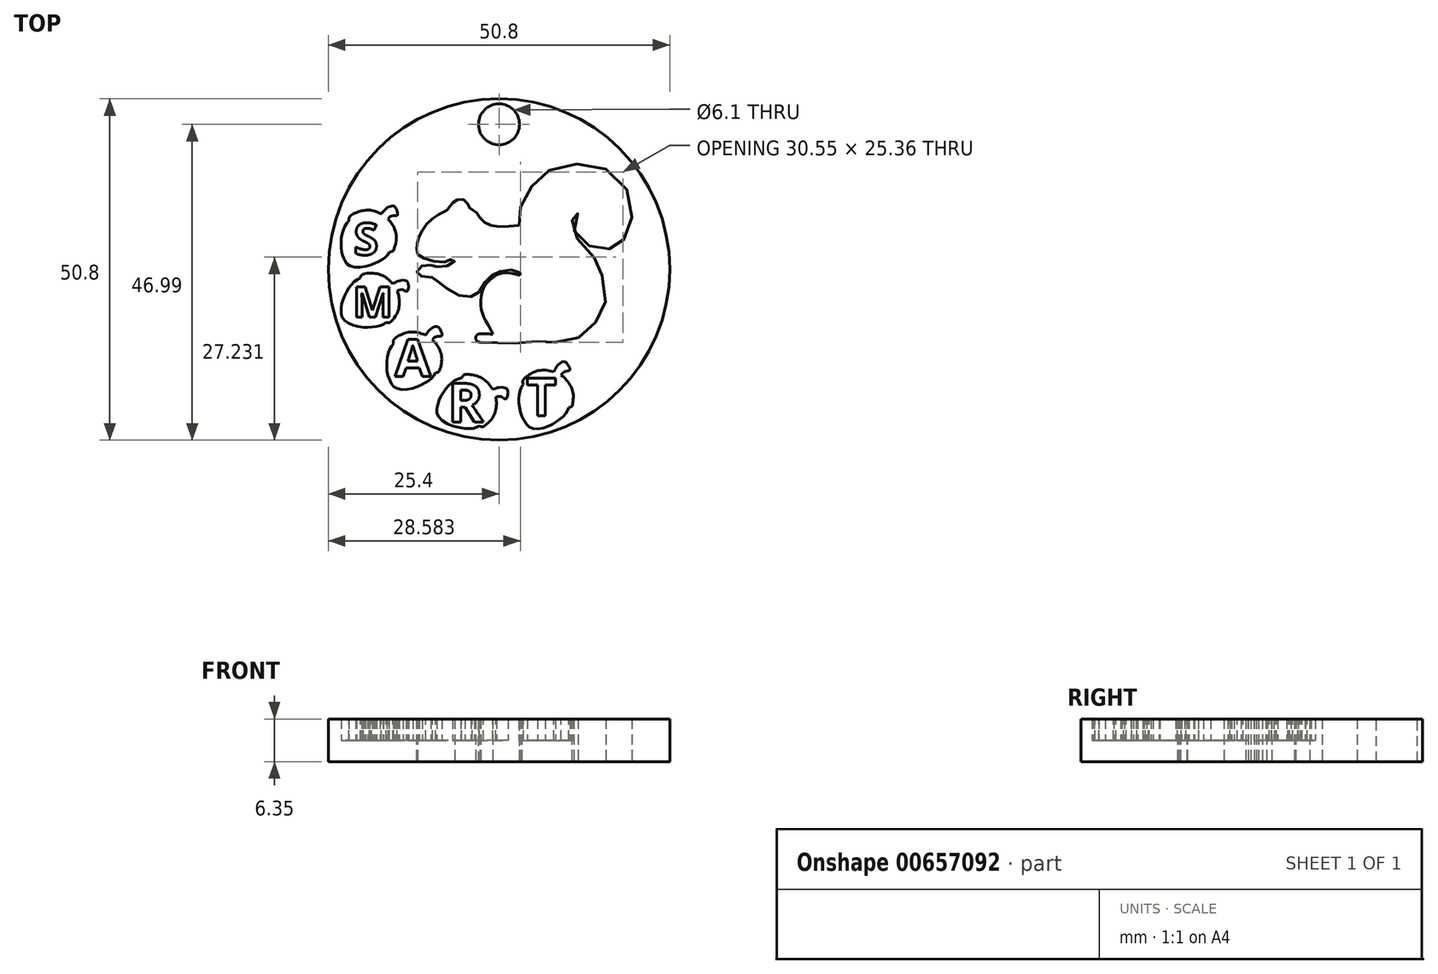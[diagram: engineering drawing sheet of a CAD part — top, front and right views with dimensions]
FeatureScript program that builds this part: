
annotation { "Feature Type Name" : "Feature", "Feature Type Description" : "" }
export const myFeature = defineFeature(function(context is Context, id is Id, definition is map)
    precondition{}
    {
        {
            var Q0;
            Q0=qCreatedBy(makeId("Top.planeOp"),FACE);
            var sketch = newSketch(context, id + "F0", { "sketchPlane" : qUnion([Q0])});
            skCircle(sketch, "E0", {"center": v(0, 0) * mm, "radius": 25.4 * mm});
            skFitSpline(sketch, "E1", {"points": [v(-12.1, 2.2) * mm, v(-12.26, 3.49) * mm, v(-11.69, 5.28) * mm, v(-10.34, 7.17) * mm, v(-8.41, 8.45) * mm, v(-7.87, 8.72) * mm, v(-7.27, 9.36) * mm, v(-6.8, 10) * mm, v(-5.44, 10.44) * mm, v(-4.57, 9.57) * mm, v(-4.2, 8.96) * mm, v(-3.55, 8.65) * mm, v(-2.64, 7.44) * mm, v(-0.82, 6.46) * mm, v(3, 6.53) * mm], "startDerivative": vector(-4.49, 18.18) * mm, "endDerivative": vector(35.45, 3.48) * mm});
            skFitSpline(sketch, "E2", {"points": [v(3, 6.53) * mm, v(3, 7.5) * mm, v(3.44, 10.07) * mm, v(4.79, 12.27) * mm, v(6.64, 14.3) * mm, v(10.15, 15.5) * mm, v(14.4, 15.47) * mm, v(18.15, 13.18) * mm, v(19.64, 9.63) * mm, v(19.47, 6.02) * mm, v(18.25, 4.06) * mm, v(17.1, 3.22) * mm, v(15.28, 3.02) * mm, v(13.33, 3.52) * mm, v(11.47, 5.08) * mm, v(11.17, 6.97) * mm, v(11.7, 8.28) * mm, v(11.74, 8.62) * mm, v(11.27, 8.32) * mm, v(10.8, 6.53) * mm, v(11.33, 4.97) * mm, v(13.66, 2.51) * mm, v(14.66, 0.7) * mm, v(15.42, -1.11) * mm, v(15.85, -4.65) * mm, v(15.06, -6.96) * mm, v(12.99, -9.3) * mm, v(11.24, -10.37) * mm, v(8.3, -10.88) * mm, v(6.28, -10.61) * mm, v(5.44, -10.76) * mm, v(3, -11) * mm, v(-2.86, -10.85) * mm], "startDerivative": vector(-1.3, 41.62) * mm, "endDerivative": vector(-127.9, 5.74) * mm});
            skFitSpline(sketch, "E3", {"points": [v(-2.86, -10.85) * mm, v(-3.36, -10.56) * mm, v(-3.44, -10.02) * mm, v(-3.08, -9.63) * mm, v(-0.95, -9.66) * mm], "startDerivative": vector(-2.88, 1) * mm, "endDerivative": vector(6.46, -0.66) * mm});
            skFitSpline(sketch, "E4", {"points": [v(-0.95, -9.66) * mm, v(-1.26, -8.87) * mm, v(-2.03, -7.56) * mm, v(-2.7, -5.53) * mm, v(-2.46, -3.21) * mm, v(-1.57, -1.76) * mm, v(0.43, -0.54) * mm, v(3.1, -0.87) * mm], "startDerivative": vector(-2.6, 7.91) * mm, "endDerivative": vector(16.1, -4.46) * mm});
            skFitSpline(sketch, "E5", {"points": [v(3.1, -0.87) * mm, v(3.4, -0.87) * mm, v(3.17, -0.52) * mm, v(2.19, -0.11) * mm, v(0.5, -0.25) * mm, v(-0.67, -0.67) * mm, v(-1.58, -1.23) * mm, v(-2.59, -2.8) * mm, v(-3.43, -3.82) * mm, v(-4.92, -4.09) * mm, v(-7.22, -3.22) * mm, v(-8.96, -1.9) * mm, v(-9.75, -1.34) * mm, v(-9.98, -1.15) * mm, v(-11.67, -1) * mm, v(-12.2, -0.62) * mm, v(-12.1, 0) * mm, v(-11.24, 0.62) * mm, v(-10.22, 0.64) * mm, v(-9.87, 0.47) * mm, v(-8.53, 0.45) * mm, v(-7.47, 0.62) * mm, v(-6.62, 1.2) * mm, v(-6.67, 1.53) * mm, v(-7.34, 1.44) * mm, v(-7.75, 1.16) * mm, v(-8.88, 1.09) * mm, v(-10.64, 1.47) * mm, v(-11.56, 1.85) * mm, v(-12.1, 2.2) * mm], "startDerivative": vector(20.9, -3.92) * mm, "endDerivative": vector(-18.16, 13.33) * mm});
            skSolve(sketch);
        }
        {
            var Q0;
            Q0=makeQuery(id+"F0.imprint","IMPRINT",FACE,{"disambiguationData":[TD([[makeQuery(id+"F0.imprint","IMPRINT",EDGE,{"derivedFrom":sQuery(id+"F0.wireOp",EDGE,"E0")}),1.0]])]});
            extrude(context, id + "F1", {"entities" : qUnion([Q0]), "depth" : 6.35 * mm, "offsetDistance" : 25.4 * mm});
        }
        {
            var Q0;
            Q0=makeQuery(id+"F1.opExtrude","CAP_FACE",FACE,{"disambiguationData":[OSD([sQuery(id+"F0.wireOp",EDGE,"E0"),sQuery(id+"F0.wireOp",EDGE,"E1"),sQuery(id+"F0.wireOp",EDGE,"E2"),sQuery(id+"F0.wireOp",EDGE,"E3"),sQuery(id+"F0.wireOp",EDGE,"E4"),sQuery(id+"F0.wireOp",EDGE,"E5")])],"isStart":false});
            var sketch = newSketch(context, id + "F2", { "sketchPlane" : qUnion([Q0])});
            skFitSpline(sketch, "E6", {"points": [v(-15.8, -2.16) * mm, v(-15.28, -1.87) * mm, v(-14.65, -1.64) * mm, v(-13.89, -1.64) * mm, v(-13.58, -1.89) * mm, v(-13.46, -2.26) * mm, v(-13.46, -2.78) * mm, v(-13.62, -3.2) * mm, v(-13.85, -3.24) * mm, v(-14.19, -3.08) * mm, v(-14.68, -3.02) * mm, v(-15.15, -3.22) * mm], "startDerivative": vector(4.96, 3.06) * mm, "endDerivative": vector(-4.83, -2.81) * mm});
            skFitSpline(sketch, "E7", {"points": [v(-15.15, -3.22) * mm, v(-15.03, -3.57) * mm, v(-14.85, -4.35) * mm, v(-14.86, -5.52) * mm, v(-15.15, -6.5) * mm, v(-15.95, -7.63) * mm, v(-16.33, -7.92) * mm, v(-16.8, -7.86) * mm], "startDerivative": vector(1.25, -3.18) * mm, "endDerivative": vector(-4.51, 1.09) * mm});
            skFitSpline(sketch, "E8", {"points": [v(-16.8, -7.86) * mm, v(-17.35, -8.24) * mm, v(-18.2, -8.5) * mm, v(-19.28, -8.61) * mm, v(-20.57, -8.56) * mm, v(-22.17, -8.14) * mm, v(-23.22, -7.29) * mm, v(-23.45, -6.6) * mm, v(-23.45, -6.04) * mm, v(-23.43, -5.4) * mm, v(-23.16, -4.37) * mm, v(-22.59, -3.14) * mm, v(-22, -2.29) * mm, v(-21.31, -1.65) * mm, v(-20.62, -1.27) * mm], "startDerivative": vector(-8.6, -6.92) * mm, "endDerivative": vector(10.97, 5.1) * mm});
            skFitSpline(sketch, "E9", {"points": [v(-20.62, -1.27) * mm, v(-20.57, -1.08) * mm, v(-20.38, -0.8) * mm, v(-19.86, -0.61) * mm, v(-19, -0.57) * mm, v(-18.25, -0.63) * mm, v(-17.39, -0.9) * mm, v(-16.63, -1.35) * mm, v(-15.8, -2.16) * mm], "startDerivative": vector(0.37, 2.7) * mm, "endDerivative": vector(5.07, -5.38) * mm});
            skFitSpline(sketch, "E10", {"points": [v(-10.93, -9.78) * mm, v(-10.59, -9.3) * mm, v(-10.11, -8.83) * mm, v(-9.42, -8.5) * mm, v(-9.04, -8.6) * mm, v(-8.78, -8.88) * mm, v(-8.56, -9.36) * mm, v(-8.52, -9.8) * mm, v(-8.7, -9.94) * mm, v(-9.08, -9.93) * mm, v(-9.56, -10.09) * mm, v(-9.9, -10.47) * mm], "startDerivative": vector(3.2, 4.87) * mm, "endDerivative": vector(-3.18, -4.59) * mm});
            skFitSpline(sketch, "E11", {"points": [v(-9.9, -10.47) * mm, v(-9.64, -10.73) * mm, v(-9.15, -11.37) * mm, v(-8.67, -12.43) * mm, v(-8.52, -13.44) * mm, v(-8.76, -14.8) * mm, v(-8.99, -15.23) * mm, v(-9.44, -15.38) * mm], "startDerivative": vector(2.48, -2.36) * mm, "endDerivative": vector(-4.55, -0.92) * mm});
            skFitSpline(sketch, "E12", {"points": [v(-9.44, -15.38) * mm, v(-9.77, -15.95) * mm, v(-10.43, -16.55) * mm, v(-11.36, -17.1) * mm, v(-12.56, -17.6) * mm, v(-14.19, -17.9) * mm, v(-15.5, -17.57) * mm, v(-16, -17.04) * mm, v(-16.23, -16.53) * mm, v(-16.48, -15.94) * mm, v(-16.67, -14.9) * mm, v(-16.67, -13.54) * mm, v(-16.5, -12.52) * mm, v(-16.15, -11.65) * mm, v(-15.68, -11.01) * mm], "startDerivative": vector(-4.86, -9.9) * mm, "endDerivative": vector(7.79, 9.25) * mm});
            skFitSpline(sketch, "E13", {"points": [v(-15.68, -11.01) * mm, v(-15.72, -10.82) * mm, v(-15.66, -10.48) * mm, v(-15.27, -10.1) * mm, v(-14.51, -9.7) * mm, v(-13.8, -9.43) * mm, v(-12.9, -9.3) * mm, v(-12.03, -9.4) * mm, v(-10.93, -9.78) * mm], "startDerivative": vector(-0.8, 2.6) * mm, "endDerivative": vector(6.87, -2.73) * mm});
            skLineSegment(sketch, "E14.0", {"start": v(-8.52, -13.44) * mm, "end": v(-9.9, -10.47) * mm, "construction": true});
            skFitSpline(sketch, "E15", {"points": [v(-0.94, -17.86) * mm, v(-0.38, -17.66) * mm, v(0.27, -17.55) * mm, v(1.02, -17.68) * mm, v(1.29, -17.97) * mm, v(1.34, -18.36) * mm, v(1.24, -18.87) * mm, v(1.02, -19.25) * mm, v(0.79, -19.26) * mm, v(0.48, -19.04) * mm, v(0, -18.9) * mm, v(-0.5, -19.01) * mm], "startDerivative": vector(5.42, 2.15) * mm, "endDerivative": vector(-5.24, -1.93) * mm});
            skFitSpline(sketch, "E16", {"points": [v(-0.5, -19.01) * mm, v(-0.43, -19.38) * mm, v(-0.39, -20.18) * mm, v(-0.6, -21.32) * mm, v(-1.06, -22.23) * mm, v(-2.04, -23.22) * mm, v(-2.47, -23.43) * mm, v(-2.93, -23.3) * mm], "startDerivative": vector(0.68, -3.35) * mm, "endDerivative": vector(-4.25, 1.86) * mm});
            skFitSpline(sketch, "E17", {"points": [v(-2.93, -23.3) * mm, v(-3.53, -23.57) * mm, v(-4.41, -23.69) * mm, v(-5.5, -23.6) * mm, v(-6.76, -23.33) * mm, v(-8.26, -22.63) * mm, v(-9.15, -21.62) * mm, v(-9.25, -20.9) * mm, v(-9.15, -20.35) * mm, v(-9.02, -19.71) * mm, v(-8.58, -18.75) * mm, v(-7.8, -17.64) * mm, v(-7.07, -16.9) * mm, v(-6.29, -16.4) * mm, v(-5.54, -16.14) * mm], "startDerivative": vector(-9.66, -5.32) * mm, "endDerivative": vector(11.68, 3.11) * mm});
            skFitSpline(sketch, "E18", {"points": [v(-5.54, -16.14) * mm, v(-5.46, -15.96) * mm, v(-5.22, -15.72) * mm, v(-4.68, -15.62) * mm, v(-3.83, -15.73) * mm, v(-3.1, -15.92) * mm, v(-2.3, -16.33) * mm, v(-1.62, -16.9) * mm, v(-0.94, -17.86) * mm], "startDerivative": vector(0.84, 2.58) * mm, "endDerivative": vector(4.06, -6.18) * mm});
            skLineSegment(sketch, "E19.0", {"start": v(-1.06, -22.23) * mm, "end": v(-0.5, -19.01) * mm, "construction": true});
            skFitSpline(sketch, "E20", {"points": [v(8.15, -15.22) * mm, v(8.42, -14.7) * mm, v(8.83, -14.17) * mm, v(9.47, -13.76) * mm, v(9.87, -13.8) * mm, v(10.16, -14.05) * mm, v(10.45, -14.49) * mm, v(10.54, -14.91) * mm, v(10.37, -15.08) * mm, v(10, -15.13) * mm, v(9.55, -15.34) * mm, v(9.26, -15.77) * mm], "startDerivative": vector(2.52, 5.26) * mm, "endDerivative": vector(-2.54, -4.98) * mm});
            skFitSpline(sketch, "E21", {"points": [v(9.26, -15.77) * mm, v(9.56, -16) * mm, v(10.13, -16.55) * mm, v(10.75, -17.54) * mm, v(11.03, -18.52) * mm, v(10.98, -19.9) * mm, v(10.81, -20.36) * mm, v(10.38, -20.57) * mm], "startDerivative": vector(2.78, -2) * mm, "endDerivative": vector(-4.38, -1.53) * mm});
            skFitSpline(sketch, "E22", {"points": [v(10.38, -20.57) * mm, v(10.13, -21.18) * mm, v(9.56, -21.86) * mm, v(8.71, -22.54) * mm, v(7.6, -23.2) * mm, v(6.02, -23.7) * mm, v(4.68, -23.56) * mm, v(4.11, -23.1) * mm, v(3.81, -22.63) * mm, v(3.48, -22.07) * mm, v(3.15, -21.07) * mm, v(2.97, -19.73) * mm, v(3, -18.69) * mm, v(3.23, -17.78) * mm, v(3.61, -17.09) * mm], "startDerivative": vector(-3.48, -10.47) * mm, "endDerivative": vector(6.47, 10.22) * mm});
            skFitSpline(sketch, "E23", {"points": [v(3.61, -17.09) * mm, v(3.55, -16.9) * mm, v(3.56, -16.56) * mm, v(3.9, -16.12) * mm, v(4.59, -15.62) * mm, v(5.26, -15.26) * mm, v(6.12, -15.02) * mm, v(7, -15) * mm, v(8.15, -15.22) * mm], "startDerivative": vector(-1.14, 2.47) * mm, "endDerivative": vector(7.18, -1.78) * mm});
            skLineSegment(sketch, "E24.0", {"start": v(11.03, -18.52) * mm, "end": v(9.26, -15.77) * mm, "construction": true});
            skFitSpline(sketch, "E25", {"points": [v(-17.5, 8.25) * mm, v(-17.14, 8.72) * mm, v(-16.64, 9.16) * mm, v(-15.94, 9.45) * mm, v(-15.56, 9.34) * mm, v(-15.31, 9.04) * mm, v(-15.11, 8.56) * mm, v(-15.1, 8.12) * mm, v(-15.3, 7.98) * mm, v(-15.67, 8) * mm, v(-16.15, 7.88) * mm, v(-16.51, 7.51) * mm], "startDerivative": vector(3.44, 4.71) * mm, "endDerivative": vector(-3.4, -4.43) * mm});
            skFitSpline(sketch, "E26", {"points": [v(-16.51, 7.51) * mm, v(-16.26, 7.24) * mm, v(-15.8, 6.58) * mm, v(-15.38, 5.5) * mm, v(-15.28, 4.48) * mm, v(-15.58, 3.13) * mm, v(-15.83, 2.72) * mm, v(-16.3, 2.59) * mm], "startDerivative": vector(2.36, -2.47) * mm, "endDerivative": vector(-4.59, -0.7) * mm});
            skFitSpline(sketch, "E27", {"points": [v(-16.3, 2.59) * mm, v(-16.65, 2.03) * mm, v(-17.33, 1.47) * mm, v(-18.3, 0.96) * mm, v(-19.51, 0.52) * mm, v(-21.15, 0.3) * mm, v(-22.45, 0.7) * mm, v(-22.92, 1.25) * mm, v(-23.12, 1.77) * mm, v(-23.35, 2.38) * mm, v(-23.5, 3.42) * mm, v(-23.43, 4.77) * mm, v(-23.2, 5.8) * mm, v(-22.8, 6.64) * mm, v(-22.3, 7.25) * mm], "startDerivative": vector(-5.34, -9.65) * mm, "endDerivative": vector(8.23, 8.86) * mm});
            skFitSpline(sketch, "E28", {"points": [v(-22.3, 7.25) * mm, v(-22.34, 7.45) * mm, v(-22.26, 7.78) * mm, v(-21.86, 8.15) * mm, v(-21.08, 8.52) * mm, v(-20.35, 8.74) * mm, v(-19.46, 8.82) * mm, v(-18.59, 8.7) * mm, v(-17.5, 8.25) * mm], "startDerivative": vector(-0.67, 2.63) * mm, "endDerivative": vector(6.73, -3.06) * mm});
            skSolve(sketch);
        }
        {
            var Q0;
            Q0=makeQuery(id+"F2.imprint","IMPRINT",FACE,{"disambiguationData":[TD([[makeQuery(id+"F2.imprint","IMPRINT",EDGE,{"derivedFrom":sQuery(id+"F2.wireOp",EDGE,"E6")}),-1.0]])]});
            var Q1;
            Q1=makeQuery(id+"F2.imprint","IMPRINT",FACE,{"disambiguationData":[TD([[makeQuery(id+"F2.imprint","IMPRINT",EDGE,{"derivedFrom":sQuery(id+"F2.wireOp",EDGE,"E10")}),-1.0]])]});
            var Q2;
            Q2=makeQuery(id+"F2.imprint","IMPRINT",FACE,{"disambiguationData":[TD([[makeQuery(id+"F2.imprint","IMPRINT",EDGE,{"derivedFrom":sQuery(id+"F2.wireOp",EDGE,"E15")}),-1.0]])]});
            var Q3;
            Q3=makeQuery(id+"F2.imprint","IMPRINT",FACE,{"disambiguationData":[TD([[makeQuery(id+"F2.imprint","IMPRINT",EDGE,{"derivedFrom":sQuery(id+"F2.wireOp",EDGE,"E20")}),-1.0]])]});
            var Q4;
            Q4=makeQuery(id+"F2.imprint","IMPRINT",FACE,{"disambiguationData":[TD([[makeQuery(id+"F2.imprint","IMPRINT",EDGE,{"derivedFrom":sQuery(id+"F2.wireOp",EDGE,"E25")}),-1.0]])]});
            extrude(context, id + "F3", {"entities" : qUnion([Q0, Q1, Q2, Q3, Q4]), "operationType" : NewBodyOperationType.REMOVE, "oppositeDirection" : true, "depth" : 3.17 * mm, "offsetDistance" : 25.4 * mm});
        }
        {
            var Q0;
            Q0=makeQuery(id+"F3.boolean.opBoolean","COPY",FACE,{"derivedFrom":makeQuery(id+"F3.opExtrude","CAP_FACE",FACE,{"disambiguationData":[OSD([sQuery(id+"F2.wireOp",EDGE,"E25"),sQuery(id+"F2.wireOp",EDGE,"E26"),sQuery(id+"F2.wireOp",EDGE,"E27"),sQuery(id+"F2.wireOp",EDGE,"E28")])],"isStart":false})});
            var sketch = newSketch(context, id + "F4", { "sketchPlane" : qUnion([Q0])});
            skText(sketch, "E29", { "text": "S", "fontName": "OpenSans-Bold.ttf"});
            skText(sketch, "E30", { "text": "M", "fontName": "OpenSans-Bold.ttf"});
            skText(sketch, "E31", { "text": "A", "fontName": "OpenSans-Bold.ttf"});
            skText(sketch, "E32", { "text": "R", "fontName": "OpenSans-Bold.ttf"});
            skText(sketch, "E33", { "text": "T", "fontName": "OpenSans-Bold.ttf"});
            const initialGuessF4  = {"E29": [-0.0216, 0.00217, 1, 0, 0.00476], "E30": [-0.02179, -0.00713, 1, 0, 0.00458], "E31": [-0.0155, -0.01596, 1, 0, 0.00557], "E32": [-0.00762, -0.0227, 1, 0, 0.0058], "E33": [0.00406, -0.02175, 1, 0, 0.0056]};
            skSetInitialGuess(sketch, initialGuessF4);
            skSolve(sketch);
        }
        {
            var Q0;
            Q0=makeQuery(id+"F4.imprint","IMPRINT",FACE,{"disambiguationData":[TD([[makeQuery(id+"F4.imprint","IMPRINT",EDGE,{"derivedFrom":sQuery(id+"F4.wireOp",EDGE,"E29.sketch_text.stroke-0")}),-1.0]])]});
            var Q1;
            Q1=makeQuery(id+"F4.imprint","IMPRINT",FACE,{"disambiguationData":[TD([[makeQuery(id+"F4.imprint","IMPRINT",EDGE,{"derivedFrom":sQuery(id+"F4.wireOp",EDGE,"E30.sketch_text.stroke-0")}),-1.0]])]});
            var Q2;
            Q2=makeQuery(id+"F4.imprint","IMPRINT",FACE,{"disambiguationData":[TD([[makeQuery(id+"F4.imprint","IMPRINT",EDGE,{"derivedFrom":sQuery(id+"F4.wireOp",EDGE,"E31.sketch_text.stroke-0")}),-1.0]])]});
            var Q3;
            Q3=makeQuery(id+"F4.imprint","IMPRINT",FACE,{"disambiguationData":[TD([[makeQuery(id+"F4.imprint","IMPRINT",EDGE,{"derivedFrom":sQuery(id+"F4.wireOp",EDGE,"E32.sketch_text.stroke-0")}),-1.0]])]});
            var Q4;
            Q4=makeQuery(id+"F4.imprint","IMPRINT",FACE,{"disambiguationData":[TD([[makeQuery(id+"F4.imprint","IMPRINT",EDGE,{"derivedFrom":sQuery(id+"F4.wireOp",EDGE,"E33.sketch_text.stroke-0")}),-1.0]])]});
            extrude(context, id + "F5", {"entities" : qUnion([Q0, Q1, Q2, Q3, Q4]), "operationType" : NewBodyOperationType.ADD, "depth" : 3.17 * mm, "offsetDistance" : 25.4 * mm});
        }
        {
            var Q0;
            Q0=makeQuery(id+"F1.opExtrude","CAP_FACE",FACE,{"disambiguationData":[OSD([sQuery(id+"F0.wireOp",EDGE,"E0"),sQuery(id+"F0.wireOp",EDGE,"E1"),sQuery(id+"F0.wireOp",EDGE,"E2"),sQuery(id+"F0.wireOp",EDGE,"E3"),sQuery(id+"F0.wireOp",EDGE,"E4"),sQuery(id+"F0.wireOp",EDGE,"E5")])],"isStart":false});
            var sketch = newSketch(context, id + "F6", { "sketchPlane" : qUnion([Q0])});
            skCircle(sketch, "E34", {"center": v(0, 71.03) * mm, "radius": 3.05 * mm});
            skCircle(sketch, "E35", {"center": v(0, 21.59) * mm, "radius": 3.05 * mm});
            skSolve(sketch);
        }
        {
            var Q0;
            Q0=makeQuery(id+"F6.imprint","IMPRINT",FACE,{"disambiguationData":[TD([[makeQuery(id+"F6.imprint","IMPRINT",EDGE,{"derivedFrom":sQuery(id+"F6.wireOp",EDGE,"E35")}),1.0]])]});
            extrude(context, id + "F7", {"entities" : qUnion([Q0]), "operationType" : NewBodyOperationType.REMOVE, "oppositeDirection" : true, "depth" : 25.4 * mm, "offsetDistance" : 25.4 * mm});
        }
    });
